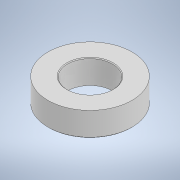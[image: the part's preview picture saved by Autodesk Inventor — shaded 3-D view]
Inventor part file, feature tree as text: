
AUTODESK INVENTOR PART (.ipt)
format: ipt  version: 2022.1 (Build 261234020, 234B)  size: 108,544 bytes
history: native  units: in
note: dims shown in document units (in); Inventor stores cm internally (conversion verified against a paired STEP export)
features: sketch x2, extrude x1, chamfer x1
ambient origin geometry x8: Origin, YZ Plane, XZ Plane, XY Plane, X Axis, Y Axis, Z Axis, Center Point
bodies: Solid1 (feature_tree)
feature tree (4):
  sketch  "Sketch1"  dims[d0=1.4in d1=0.75in d2=0.4in d3=0.0in]
  extrude  "Extrusion1"  Depth=0.4in
  chamfer  "Chamfer1"  Distance=0.4in
  sketch  "Sketch2"  dims[d4=0.0125in d5=0.125in d6=45.0deg]
